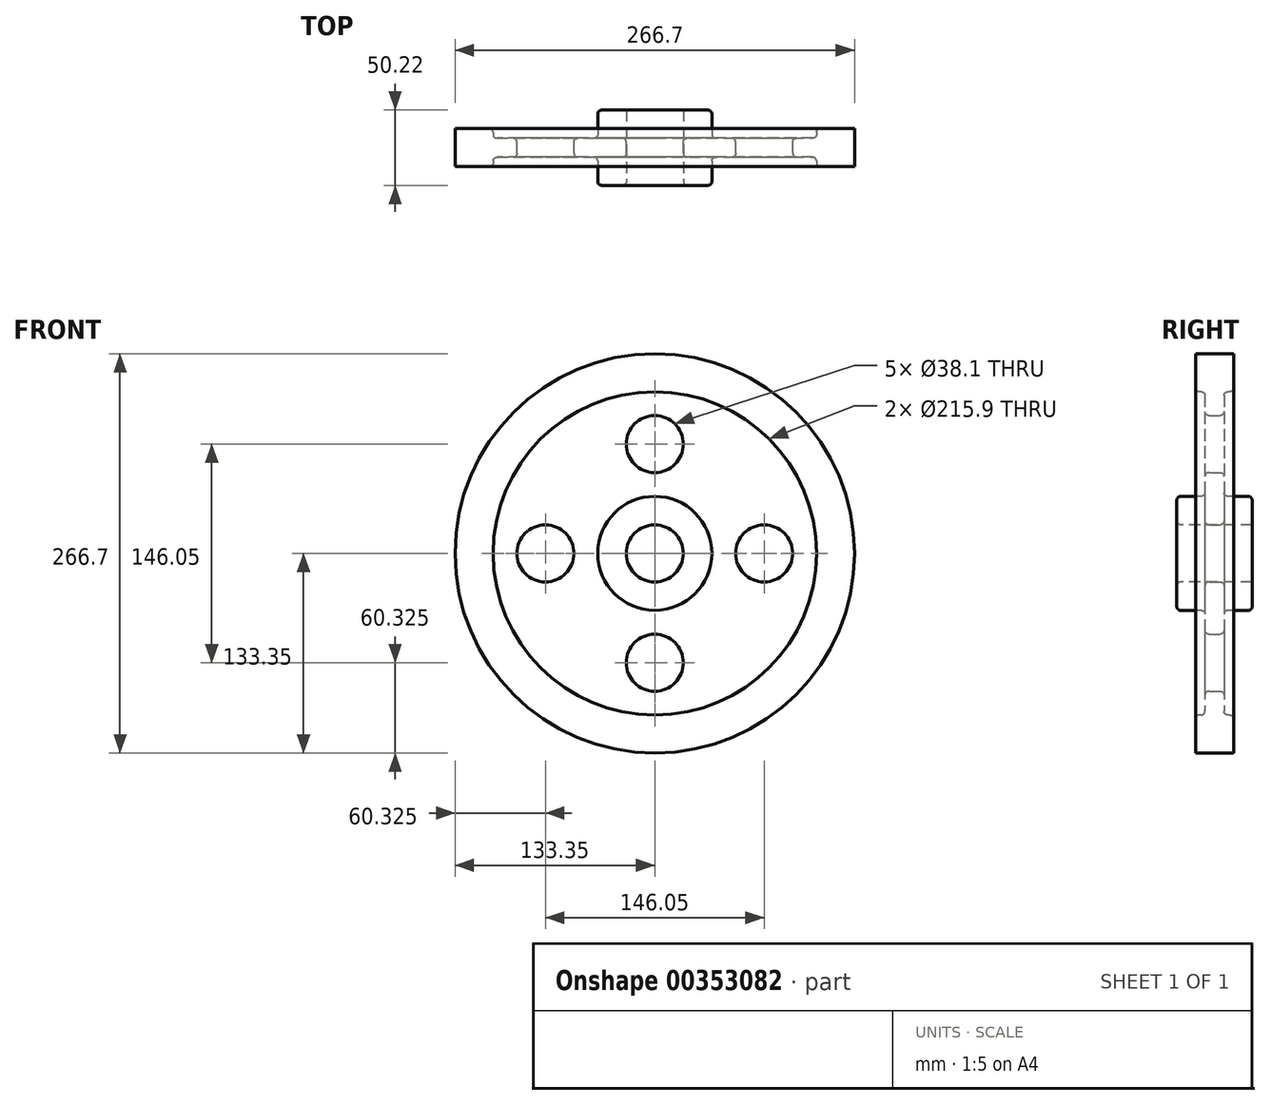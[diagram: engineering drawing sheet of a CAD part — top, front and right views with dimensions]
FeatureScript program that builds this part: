
annotation { "Feature Type Name" : "Feature", "Feature Type Description" : "" }
export const myFeature = defineFeature(function(context is Context, id is Id, definition is map)
    precondition{}
    {
        {
            var Q0;
            Q0=qCreatedBy(makeId("Right.planeOp"),FACE);
            var sketch = newSketch(context, id + "F0", { "sketchPlane" : qUnion([Q0])});
            skLineSegment(sketch, "E0", {"start": v(0, 0) * mm, "end": v(12.7, 0) * mm});
            skLineSegment(sketch, "E1.0", {"start": v(0, 19.05) * mm, "end": v(25.4, 19.05) * mm});
            skLineSegment(sketch, "E2.0", {"start": v(0, 38.1) * mm, "end": v(25.4, 38.1) * mm});
            skLineSegment(sketch, "E3.0", {"start": v(0, 73.03) * mm, "end": v(12.7, 73.03) * mm});
            skLineSegment(sketch, "E4.0", {"start": v(0, 107.95) * mm, "end": v(12.7, 107.95) * mm});
            skLineSegment(sketch, "E5.0", {"start": v(0, 133.35) * mm, "end": v(12.7, 133.35) * mm});
            skLineSegment(sketch, "E6", {"start": v(0, 133.35) * mm, "end": v(0, 0) * mm});
            skLineSegment(sketch, "E7.0", {"start": v(25.4, 108.24) * mm, "end": v(25.4, 107.95) * mm});
            skLineSegment(sketch, "E8.0", {"start": v(25.1, 108.24) * mm, "end": v(25.1, 107.95) * mm});
            skLineSegment(sketch, "E8.1", {"start": v(25.1, 108.24) * mm, "end": v(25.4, 108.24) * mm});
            skLineSegment(sketch, "E9.0", {"start": v(6.35, 107.95) * mm, "end": v(6.35, 38.1) * mm});
            skLineSegment(sketch, "E10.0", {"start": v(12.7, 133.35) * mm, "end": v(12.7, 107.95) * mm});
            skLineSegment(sketch, "E11.trimOffspring", {"start": v(25.1, 38.1) * mm, "end": v(25.1, 19.05) * mm});
            skLineSegment(sketch, "E12.trimOffspring", {"start": v(25.4, 38.1) * mm, "end": v(25.4, 19.05) * mm});
            skLineSegment(sketch, "E13.trimOffspring", {"start": v(25.1, 107.95) * mm, "end": v(25.4, 107.95) * mm});
            skLineSegment(sketch, "E14.trimOffspring", {"start": v(25.1, 0) * mm, "end": v(76.2, 0) * mm});
            skLineSegment(sketch, "E15.MirrorCS", {"start": v(-12.7, 133.35) * mm, "end": v(-12.7, 107.95) * mm});
            skLineSegment(sketch, "E16.MirrorCS", {"start": v(-6.35, 107.95) * mm, "end": v(-6.35, 38.1) * mm});
            skLineSegment(sketch, "E17.MirrorCS", {"start": v(0, 38.1) * mm, "end": v(-25.4, 38.1) * mm});
            skLineSegment(sketch, "E18.MirrorCS", {"start": v(0, 19.05) * mm, "end": v(-25.4, 19.05) * mm});
            skLineSegment(sketch, "E19.MirrorCS", {"start": v(-25.1, 38.1) * mm, "end": v(-25.1, 19.05) * mm});
            skLineSegment(sketch, "E20.MirrorCS", {"start": v(0, 107.95) * mm, "end": v(-12.7, 107.95) * mm});
            skLineSegment(sketch, "E21.MirrorCS", {"start": v(0, 133.35) * mm, "end": v(-12.7, 133.35) * mm});
            skPoint(sketch, "E22.orphan", {"position": v(-6.35, 133.35) * mm});
            skPoint(sketch, "E23.orphan", {"position": v(6.35, 133.35) * mm});
            skPoint(sketch, "E24.trimOffspring.end.orphan", {"position": v(12.7, 19.05) * mm});
            skPoint(sketch, "E24.trimOffspring.start.orphan", {"position": v(12.7, 38.1) * mm});
            skPoint(sketch, "E25.orphan", {"position": v(6.35, 19.05) * mm});
            skPoint(sketch, "E26.orphan", {"position": v(-6.35, 19.05) * mm});
            skPoint(sketch, "E27.MirrorCS.end.orphan", {"position": v(-12.7, 19.05) * mm});
            skPoint(sketch, "E27.MirrorCS.start.orphan", {"position": v(-12.7, 38.1) * mm});
            skSolve(sketch);
        }
        {
            var Q0;
            {var subQ4=sQuery(id+"F0.wireOp",EDGE,"E15.MirrorCS");Q0=makeQuery(id+"F0.imprint","IMPRINT",FACE,{"disambiguationData":[TD([[makeQuery(id+"F0.imprint","IMPRINT",EDGE,{"derivedFrom":subQ4}),1.0]])]});}
            var Q1;
            {var subQ3=sQuery(id+"F0.wireOp",EDGE,"E5.0");Q1=makeQuery(id+"F0.imprint","IMPRINT",FACE,{"disambiguationData":[TD([[makeQuery(id+"F0.imprint","IMPRINT",EDGE,{"derivedFrom":subQ3}),-1.0]])]});}
            var Q2;
            {var subQ3=sQuery(id+"F0.wireOp",EDGE,"E16.MirrorCS");Q2=makeQuery(id+"F0.imprint","IMPRINT",FACE,{"disambiguationData":[TD([[makeQuery(id+"F0.imprint","IMPRINT",EDGE,{"derivedFrom":subQ3}),1.0]])]});}
            var Q3;
            {var subQ0=sQuery(id+"F0.wireOp",EDGE,"E6");var subQ1=sQuery(id+"F0.wireOp",EDGE,"E3.0");var subQ2=makeQuery(id+"F0.imprint","INTERSECT",VERTEX,{"derivedFrom":[subQ1,subQ0]});Q3=makeQuery(id+"F0.imprint","IMPRINT",FACE,{"disambiguationData":[TD([[makeQuery(id+"F0.imprint","IMPRINT",EDGE,{"disambiguationData":[TD([[subQ2,-1.0]])],"derivedFrom":subQ1}),1.0]])]});}
            var Q4;
            {var subQ0=sQuery(id+"F0.wireOp",EDGE,"E6");var subQ5=sQuery(id+"F0.wireOp",EDGE,"E3.0");var subQ7=makeQuery(id+"F0.imprint","INTERSECT",VERTEX,{"derivedFrom":[subQ5,subQ0]});Q4=makeQuery(id+"F0.imprint","IMPRINT",FACE,{"disambiguationData":[TD([[makeQuery(id+"F0.imprint","IMPRINT",EDGE,{"disambiguationData":[TD([[subQ7,-1.0]])],"derivedFrom":subQ5}),-1.0]])]});}
            var Q5;
            {var subQ3=sQuery(id+"F0.wireOp",EDGE,"E19.MirrorCS");Q5=makeQuery(id+"F0.imprint","IMPRINT",FACE,{"disambiguationData":[TD([[makeQuery(id+"F0.imprint","IMPRINT",EDGE,{"derivedFrom":subQ3}),1.0]])]});}
            var Q6;
            {var subQ2=sQuery(id+"F0.wireOp",EDGE,"E11.trimOffspring");Q6=makeQuery(id+"F0.imprint","IMPRINT",FACE,{"disambiguationData":[TD([[makeQuery(id+"F0.imprint","IMPRINT",EDGE,{"derivedFrom":subQ2}),-1.0]])]});}
            var Q7;
            Q7=sQuery(id+"F0.wireOp",EDGE,"E0");
            revolve(context, id + "F1", {"entities" : qUnion([Q0, Q1, Q2, Q3, Q4, Q5, Q6]), "axis" : qUnion([Q7]), "revolveType" : RevolveType.FULL});
        }
        {
            var Q0;
            Q0=makeQuery(id+"F1.opRevolve","SWEPT_FACE",FACE,{"disambiguationData":[OSD([sQuery(id+"F0.wireOp",EDGE,"E9.0")])]});
            var sketch = newSketch(context, id + "F2", { "sketchPlane" : qUnion([Q0])});
            skLineSegment(sketch, "E28", {"start": v(0, 0) * mm, "end": v(0, 73.03) * mm});
            skCircle(sketch, "E29", {"center": v(0, 73.03) * mm, "radius": 19.05 * mm});
            skCircle(sketch, "E30.1.0", {"center": v(-73.03, 0) * mm, "radius": 19.05 * mm});
            skCircle(sketch, "E30.2.0", {"center": v(0, -73.03) * mm, "radius": 19.05 * mm});
            skCircle(sketch, "E30.3.0", {"center": v(73.03, 0) * mm, "radius": 19.05 * mm});
            skPoint(sketch, "E30.center", {"position": v(0, 0) * mm});
            skSolve(sketch);
        }
        {
            var Q0;
            Q0 = qSketchRegion(id + "F2", true);
            extrude(context, id + "F3", {"entities" : qUnion([Q0]), "operationType" : NewBodyOperationType.REMOVE, "oppositeDirection" : true, "depth" : 25.4 * mm});
        }
        {
            var Q0;
            Q0=makeQuery(id+"F1.opRevolve","SWEPT_FACE",FACE,{"disambiguationData":[OSD([sQuery(id+"F0.wireOp",EDGE,"E20.MirrorCS")])]});
            var Q1;
            Q1=makeQuery(id+"F1.opRevolve","SWEPT_FACE",FACE,{"disambiguationData":[OSD([sQuery(id+"F0.wireOp",EDGE,"E16.MirrorCS")])]});
            var Q2;
            Q2=makeQuery(id+"F1.opRevolve","SWEPT_FACE",FACE,{"disambiguationData":[OSD([sQuery(id+"F0.wireOp",EDGE,"E17.MirrorCS")])]});
            var Q3;
            Q3=makeQuery(id+"F1.opRevolve","SWEPT_FACE",FACE,{"disambiguationData":[OSD([sQuery(id+"F0.wireOp",EDGE,"E19.MirrorCS")])]});
            fillet(context, id + "F4", {"entities" : qUnion([Q0, Q1, Q2, Q3]), "radius" : 2.54 * mm, "tangentPropagation" : true, "allowEdgeOverflow" : false});
        }
        {
            var Q0;
            Q0=makeQuery(id+"F1.opRevolve","SWEPT_EDGE",EDGE,{"disambiguationData":[OSD([sQuery(id+"F0.wireOp",EDGE,"E4.0"),sQuery(id+"F0.wireOp",EDGE,"E10.0")])]});
            var Q1;
            Q1=makeQuery(id+"F1.opRevolve","SWEPT_FACE",FACE,{"disambiguationData":[OSD([sQuery(id+"F0.wireOp",EDGE,"E9.0")])]});
            var Q2;
            Q2=makeQuery(id+"F1.opRevolve","SWEPT_EDGE",EDGE,{"disambiguationData":[OSD([sQuery(id+"F0.wireOp",EDGE,"E2.0"),sQuery(id+"F0.wireOp",EDGE,"E11.trimOffspring")])]});
            fillet(context, id + "F5", {"entities" : qUnion([Q0, Q1, Q2]), "radius" : 2.54 * mm, "tangentPropagation" : true, "allowEdgeOverflow" : false});
        }
    });
